# Revit family: P1001
name_source: partatom
category: Generic Models
units: mm (PartAtom-declared; Revit-internal decimal feet)

## family parameters
Can host rebar = No
Cut with Voids When Loaded = No
Part Type = Normal
Room Calculation Point = No
Round Connector Dimension = Use Diameter
Shared = No

## types (7) — shared parameters
Description = P1001 - 1-5/8 x 3-1/4 - 12 Gauge Back-to-Back Solid - GenericModels
Height = 3.250"
Manufacturer = Atkore Unistrut
Model = P1001
Salsify ID1 = US-P1001
URL = https://www.atkore.com
zero-valued in all types: Default Elevation

## per-type parameters (varying)
| type | Material | Power-Strut Part Number | UPC-10ft | UPC-20ft | Unit Weight |
| P1001 SS | Stainless Steel | PS 200 2T3 SS | "0786364014012" | "786364014074" | 3.84 lb/ft |
| P1001 ZD | Zinc Dichromate |  | "786364057514" | "786364057521" | 3.84 lb/ft |
| P1001 PG | Pre-Galvanized | PS 200 2T3 PGAL | "0786364100319" | "0786364100302" | 3.84 lb/ft |
| P1001 PL | Plain |  | "786364014005" | "786364014067" | 3.84 lb/ft |
| P1001 ST | Stainless Steel | PS 200 2T3 ST | "0786364907895" | "786364014081" | 3.8 lb/ft |
| P1001 GR | Green | PS 200 2T3 GRN | "0786364100111" | "0786364100104" | 3.84 lb/ft |
| P1001 DF | Defender |  | "786364051802" | "786364051819" | 3.8 lb/ft |

note: column(s) folded — value = type name in every type: Part Number

## geometry (parser evidence)
native form markers: Sweep x5
no freeform markers — native parametric forms only
